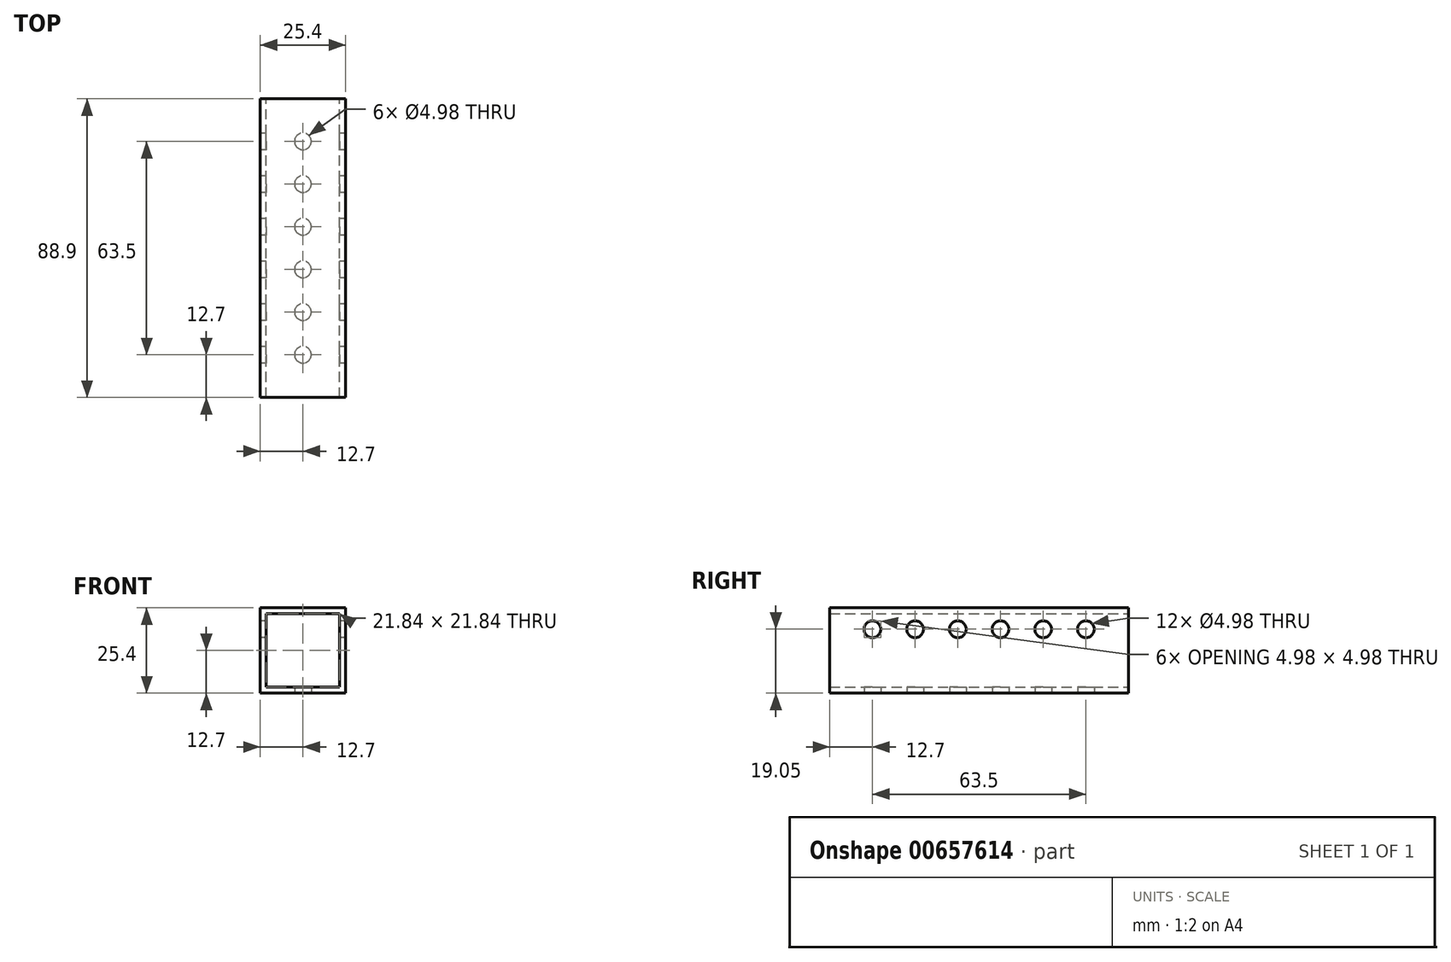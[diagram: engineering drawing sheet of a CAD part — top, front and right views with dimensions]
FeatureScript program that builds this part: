
annotation { "Feature Type Name" : "Feature", "Feature Type Description" : "" }
export const myFeature = defineFeature(function(context is Context, id is Id, definition is map)
    precondition{}
    {
        {
            var Q0;
            Q0=qCreatedBy(makeId("Front.planeOp"),FACE);
            var sketch = newSketch(context, id + "F0", { "sketchPlane" : qUnion([Q0])});
            skLineSegment(sketch, "E0.bottom", {"start": v(0, 0) * mm, "end": v(-25.4, 0) * mm});
            skLineSegment(sketch, "E0.top", {"start": v(0, 25.4) * mm, "end": v(-25.4, 25.4) * mm});
            skLineSegment(sketch, "E0.left", {"start": v(0, 0) * mm, "end": v(0, 25.4) * mm});
            skLineSegment(sketch, "E0.right", {"start": v(-25.4, 0) * mm, "end": v(-25.4, 25.4) * mm});
            skLineSegment(sketch, "E1.bottom", {"start": v(-23.62, 23.62) * mm, "end": v(-1.78, 23.62) * mm});
            skLineSegment(sketch, "E1.top", {"start": v(-23.62, 1.78) * mm, "end": v(-1.78, 1.78) * mm});
            skLineSegment(sketch, "E1.left", {"start": v(-23.62, 23.62) * mm, "end": v(-23.62, 1.78) * mm});
            skLineSegment(sketch, "E1.right", {"start": v(-1.78, 23.62) * mm, "end": v(-1.78, 1.78) * mm});
            skSolve(sketch);
        }
        {
            var Q0;
            Q0=makeQuery(id+"F0.imprint","IMPRINT",FACE,{"disambiguationData":[TD([[makeQuery(id+"F0.imprint","IMPRINT",EDGE,{"derivedFrom":sQuery(id+"F0.wireOp",EDGE,"E0.bottom")}),-1.0]])]});
            extrude(context, id + "F1", {"entities" : qUnion([Q0]), "depth" : 88.9 * mm, "offsetDistance" : 25.4 * mm});
        }
        {
            var Q0;
            Q0=makeQuery(id+"F1.opExtrude","SWEPT_FACE",FACE,{"disambiguationData":[OSD([sQuery(id+"F0.wireOp",EDGE,"E0.right")])]});
            var sketch = newSketch(context, id + "F2", { "sketchPlane" : qUnion([Q0])});
            skCircle(sketch, "E2", {"center": v(12.7, 19.05) * mm, "radius": 2.49 * mm});
            skCircle(sketch, "E3.1.0.0", {"center": v(25.4, 19.05) * mm, "radius": 2.49 * mm});
            skCircle(sketch, "E3.2.0.0", {"center": v(38.1, 19.05) * mm, "radius": 2.49 * mm});
            skCircle(sketch, "E3.3.0.0", {"center": v(50.8, 19.05) * mm, "radius": 2.49 * mm});
            skCircle(sketch, "E3.4.0.0", {"center": v(63.5, 19.05) * mm, "radius": 2.49 * mm});
            skCircle(sketch, "E3.5.0.0", {"center": v(76.2, 19.05) * mm, "radius": 2.49 * mm});
            skLineSegment(sketch, "E3.direction1", {"start": v(12.7, 19.05) * mm, "end": v(25.4, 19.05) * mm, "construction": true});
            skSolve(sketch);
        }
        {
            var Q0;
            Q0 = qSketchRegion(id + "F2", true);
            extrude(context, id + "F3", {"entities" : qUnion([Q0]), "operationType" : NewBodyOperationType.REMOVE, "oppositeDirection" : true, "depth" : 25.4 * mm, "offsetDistance" : 25.4 * mm});
        }
        {
            var Q0;
            Q0=makeQuery(id+"F1.opExtrude","SWEPT_FACE",FACE,{"disambiguationData":[OSD([sQuery(id+"F0.wireOp",EDGE,"E0.bottom")])]});
            var sketch = newSketch(context, id + "F4", { "sketchPlane" : qUnion([Q0])});
            skCircle(sketch, "E4", {"center": v(-12.7, 76.2) * mm, "radius": 2.49 * mm});
            skCircle(sketch, "E5.0.1.0", {"center": v(-12.7, 63.5) * mm, "radius": 2.49 * mm});
            skCircle(sketch, "E5.0.2.0", {"center": v(-12.7, 50.8) * mm, "radius": 2.49 * mm});
            skCircle(sketch, "E5.0.3.0", {"center": v(-12.7, 38.1) * mm, "radius": 2.49 * mm});
            skCircle(sketch, "E5.0.4.0", {"center": v(-12.7, 25.4) * mm, "radius": 2.49 * mm});
            skCircle(sketch, "E5.0.5.0", {"center": v(-12.7, 12.7) * mm, "radius": 2.49 * mm});
            skLineSegment(sketch, "E5.direction1", {"start": v(-12.7, 76.2) * mm, "end": v(12.7, 76.2) * mm, "construction": true});
            skLineSegment(sketch, "E5.direction2", {"start": v(-12.7, 76.2) * mm, "end": v(-12.7, 63.5) * mm, "construction": true});
            skSolve(sketch);
        }
        {
            var Q0;
            Q0 = qSketchRegion(id + "F4", true);
            extrude(context, id + "F5", {"entities" : qUnion([Q0]), "operationType" : NewBodyOperationType.REMOVE, "endBound" : BoundingType.UP_TO_NEXT, "oppositeDirection" : true, "depth" : 25.4 * mm, "offsetDistance" : 25.4 * mm});
        }
    });
